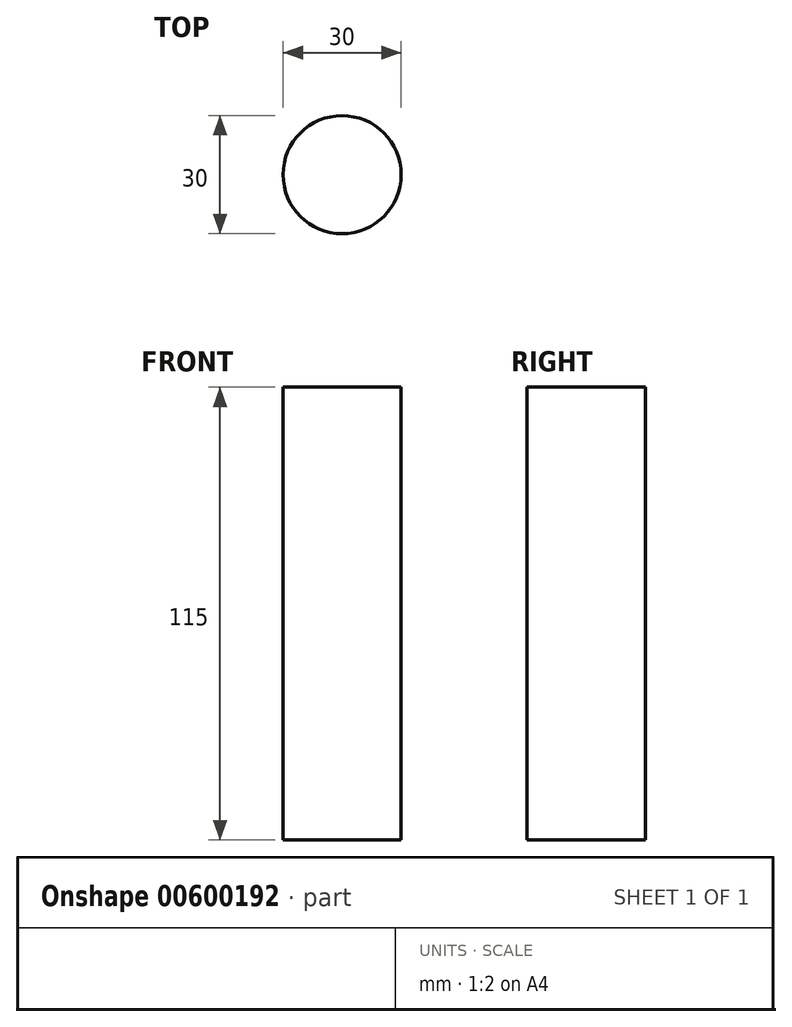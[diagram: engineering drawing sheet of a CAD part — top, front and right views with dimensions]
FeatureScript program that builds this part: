
annotation { "Feature Type Name" : "Feature", "Feature Type Description" : "" }
export const myFeature = defineFeature(function(context is Context, id is Id, definition is map)
    precondition{}
    {
        {
            var Q0;
            Q0=qCreatedBy(makeId("Top.planeOp"),FACE);
            var sketch = newSketch(context, id + "F0", { "sketchPlane" : qUnion([Q0])});
            skCircle(sketch, "E0", {"center": v(0, 0) * mm, "radius": 15 * mm});
            skSolve(sketch);
        }
        {
            var Q0;
            Q0 = qSketchRegion(id + "F0", true);
            extrude(context, id + "F1", {"entities" : qUnion([Q0]), "depth" : 115 * mm, "offsetDistance" : 25 * mm});
        }
    });
